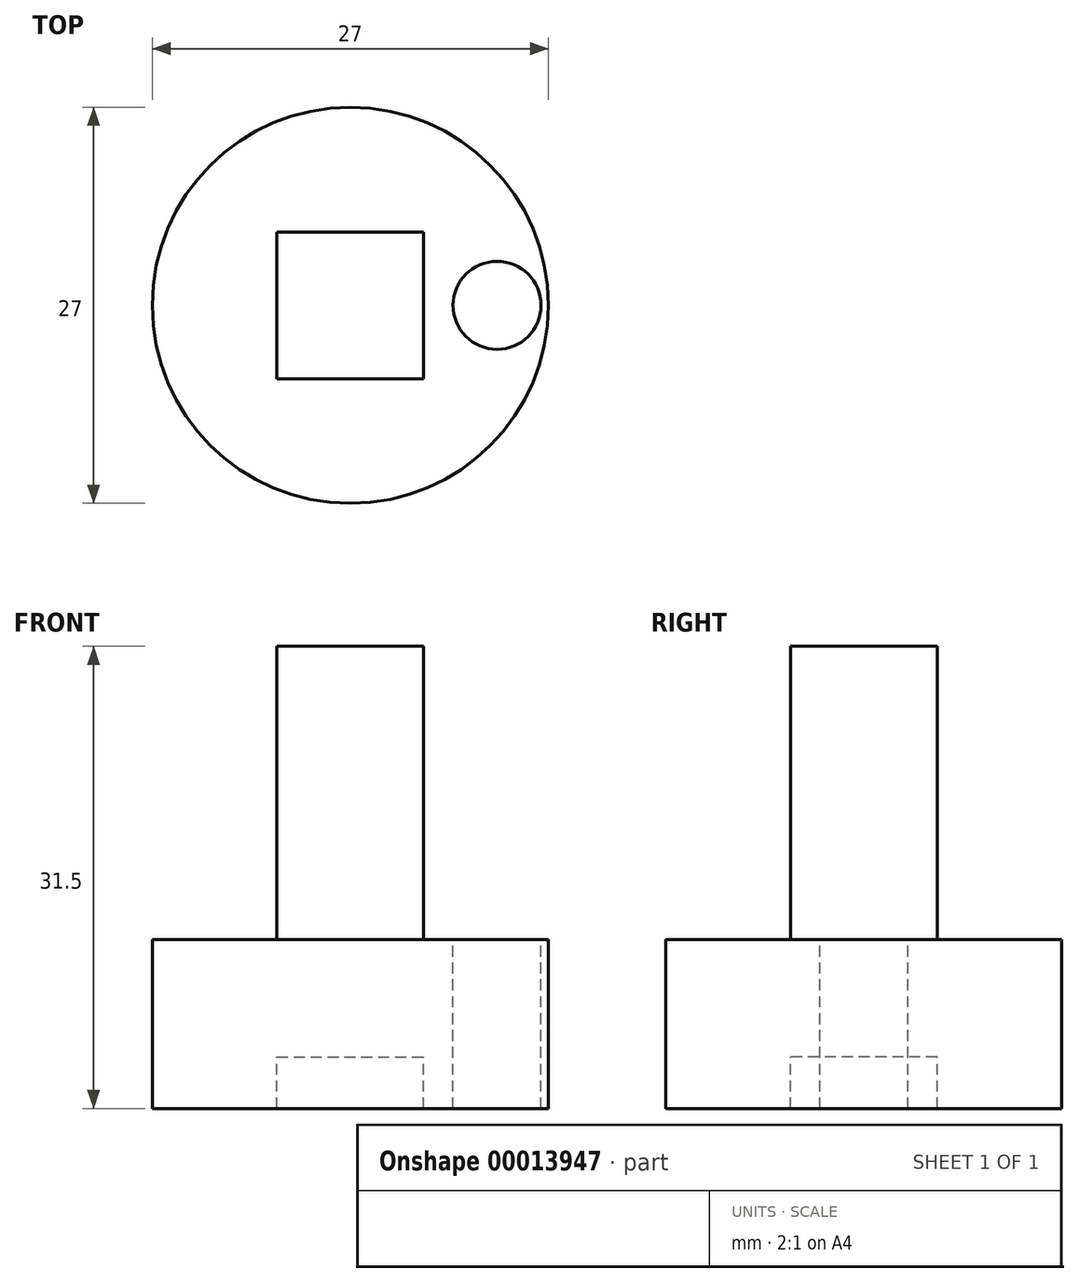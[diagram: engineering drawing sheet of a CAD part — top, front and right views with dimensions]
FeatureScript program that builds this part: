
annotation { "Feature Type Name" : "Feature", "Feature Type Description" : "" }
export const myFeature = defineFeature(function(context is Context, id is Id, definition is map)
    precondition{}
    {
        {
            var Q0;
            Q0=qCreatedBy(makeId("Top.planeOp"),FACE);
            var sketch = newSketch(context, id + "F0", { "sketchPlane" : qUnion([Q0])});
            skCircle(sketch, "E0", {"center": v(0, 0) * mm, "radius": 13.5 * mm});
            skCircle(sketch, "E1", {"center": v(-10, 0) * mm, "radius": 3 * mm});
            skCircle(sketch, "E2.MirrorC", {"center": v(10, 0) * mm, "radius": 3 * mm});
            skLineSegment(sketch, "E3.rect.bottom", {"start": v(5, -5) * mm, "end": v(-5, -5) * mm});
            skLineSegment(sketch, "E3.rect.top", {"start": v(5, 5) * mm, "end": v(-5, 5) * mm});
            skLineSegment(sketch, "E3.rect.left", {"start": v(5, -5) * mm, "end": v(5, 5) * mm});
            skLineSegment(sketch, "E3.rect.right", {"start": v(-5, -5) * mm, "end": v(-5, 5) * mm});
            skSolve(sketch);
        }
        {
            var Q0;
            Q0=makeQuery(id+"F0.imprint","IMPRINT",FACE,{"disambiguationData":[TD([[makeQuery(id+"F0.imprint","IMPRINT",EDGE,{"derivedFrom":sQuery(id+"F0.wireOp",EDGE,"E1")}),1.0]])]});
            extrude(context, id + "F1", {"entities" : qUnion([Q0]), "oppositeDirection" : true, "depth" : 3.5 * mm, "hasSecondDirection" : true, "secondDirectionOppositeDirection" : false, "secondDirectionDepth" : 8 * mm});
        }
        {
            var Q0;
            Q0=makeQuery(id+"F0.imprint","IMPRINT",FACE,{"disambiguationData":[TD([[makeQuery(id+"F0.imprint","IMPRINT",EDGE,{"derivedFrom":sQuery(id+"F0.wireOp",EDGE,"E2.MirrorC")}),-1.0]])]});
            var Q1;
            Q1=sQuery(id+"F0.wireOp",EDGE,"E2.MirrorC");
            extrude(context, id + "F2", {"entities" : qUnion([Q0]), "surfaceEntities" : qUnion([Q1]), "oppositeDirection" : true, "depth" : 3.5 * mm, "hasSecondDirection" : true, "secondDirectionOppositeDirection" : false, "secondDirectionDepth" : 8 * mm});
        }
        {
            var Q0;
            Q0=makeQuery(id+"F0.imprint","IMPRINT",FACE,{"disambiguationData":[TD([[makeQuery(id+"F0.imprint","IMPRINT",EDGE,{"derivedFrom":sQuery(id+"F0.wireOp",EDGE,"E3.rect.bottom")}),-1.0]])]});
            var Q1;
            Q1=sQuery(id+"F0.wireOp",EDGE,"E0");
            extrude(context, id + "F3", {"entities" : qUnion([Q0]), "surfaceEntities" : qUnion([Q1]), "depth" : 28 * mm});
        }
        {
            var Q0;
            Q0=makeQuery(id+"F0.imprint","IMPRINT",FACE,{"disambiguationData":[TD([[makeQuery(id+"F0.imprint","IMPRINT",EDGE,{"derivedFrom":sQuery(id+"F0.wireOp",EDGE,"E0")}),1.0]])]});
            var Q1;
            Q1=sQuery(id+"F0.wireOp",EDGE,"E0");
            extrude(context, id + "F4", {"entities" : qUnion([Q0]), "surfaceEntities" : qUnion([Q1]), "depth" : 8 * mm});
        }
        {
            var Q0;
            Q0=makeQuery(id+"F1.opExtrude","SWEPT_BODY",BODY,{"disambiguationData":[OSD([sQuery(id+"F0.wireOp",EDGE,"E1")])]});
            var Q1;
            Q1=makeQuery(id+"F2.opExtrude","SWEPT_BODY",BODY,{"disambiguationData":[OSD([sQuery(id+"F0.wireOp",EDGE,"E2.MirrorC")])]});
            var Q2;
            Q2=makeQuery(id+"F3.opExtrude","SWEPT_BODY",BODY,{"disambiguationData":[OSD([sQuery(id+"F0.wireOp",EDGE,"E3.rect.bottom"),sQuery(id+"F0.wireOp",EDGE,"E3.rect.top"),sQuery(id+"F0.wireOp",EDGE,"E3.rect.left"),sQuery(id+"F0.wireOp",EDGE,"E3.rect.right")])]});
            var Q3;
            Q3=makeQuery(id+"F4.opExtrude","SWEPT_BODY",BODY,{"disambiguationData":[OSD([sQuery(id+"F0.wireOp",EDGE,"E0"),sQuery(id+"F0.wireOp",EDGE,"E1"),sQuery(id+"F0.wireOp",EDGE,"E2.MirrorC"),sQuery(id+"F0.wireOp",EDGE,"E3.rect.bottom"),sQuery(id+"F0.wireOp",EDGE,"E3.rect.top"),sQuery(id+"F0.wireOp",EDGE,"E3.rect.left"),sQuery(id+"F0.wireOp",EDGE,"E3.rect.right")])]});
            booleanBodies(context, id + "F5", {"operationType" : BooleanOperationType.UNION, "tools" : qUnion([Q0, Q1, Q2, Q3])});
        }
    });
